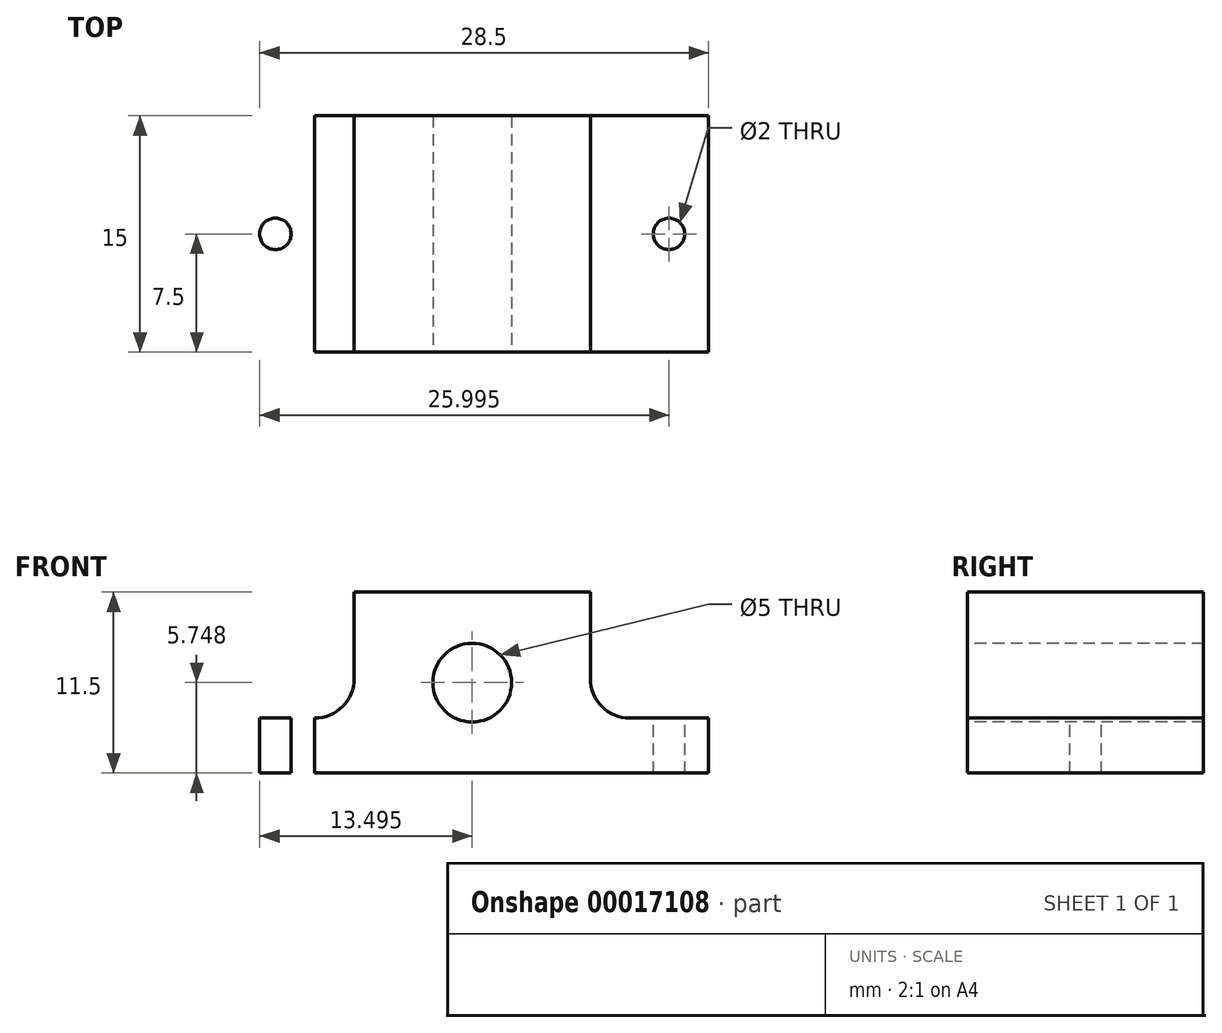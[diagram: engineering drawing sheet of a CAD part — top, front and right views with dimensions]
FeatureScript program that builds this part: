
annotation { "Feature Type Name" : "Feature", "Feature Type Description" : "" }
export const myFeature = defineFeature(function(context is Context, id is Id, definition is map)
    precondition{}
    {
        {
            var Q0;
            Q0=qCreatedBy(makeId("Front.planeOp"),FACE);
            var sketch = newSketch(context, id + "F0", { "sketchPlane" : qUnion([Q0])});
            skLineSegment(sketch, "E0", {"start": v(-8.65, 8.43) * mm, "end": v(6.35, 8.43) * mm});
            skLineSegment(sketch, "E1", {"start": v(6.35, 8.43) * mm, "end": v(6.35, 2.93) * mm});
            skLineSegment(sketch, "E2", {"start": v(8.85, 0.43) * mm, "end": v(13.85, 0.43) * mm});
            skLineSegment(sketch, "E3", {"start": v(13.85, 0.43) * mm, "end": v(13.85, -3.07) * mm});
            skLineSegment(sketch, "E4", {"start": v(-8.65, 8.43) * mm, "end": v(-8.65, 2.93) * mm});
            skLineSegment(sketch, "E5", {"start": v(-11.15, 0.43) * mm, "end": v(-16.15, 0.43) * mm});
            skLineSegment(sketch, "E6", {"start": v(-16.15, 0.43) * mm, "end": v(-16.15, -3.07) * mm});
            skLineSegment(sketch, "E7", {"start": v(-16.15, -3.07) * mm, "end": v(13.85, -3.07) * mm});
            skPoint(sketch, "E8.visualSharp", {"position": v(6.35, 0.43) * mm});
            skArc(sketch, "E8.filletArc", {"start": v(6.35, 2.93) * mm, "mid": v(7.08, 1.16) * mm, "end": v(8.85, 0.43) * mm});
            skPoint(sketch, "E9.visualSharp", {"position": v(-8.65, 0.43) * mm});
            skArc(sketch, "E9.filletArc", {"start": v(-11.15, 0.43) * mm, "mid": v(-9.39, 1.16) * mm, "end": v(-8.65, 2.93) * mm});
            skSolve(sketch);
        }
        {
            var Q0;
            Q0=makeQuery(id+"F0.imprint","IMPRINT",FACE,{"disambiguationData":[TD([[makeQuery(id+"F0.imprint","IMPRINT",EDGE,{"derivedFrom":sQuery(id+"F0.wireOp",EDGE,"E0")}),-1.0]])]});
            extrude(context, id + "F1", {"entities" : qUnion([Q0]), "depth" : 15 * mm});
        }
        {
            var Q0;
            Q0=makeQuery(id+"F1.opExtrude","SWEPT_FACE",FACE,{"disambiguationData":[OSD([sQuery(id+"F0.wireOp",EDGE,"E2")])]});
            var sketch = newSketch(context, id + "F2", { "sketchPlane" : qUnion([Q0])});
            skCircle(sketch, "E10", {"center": v(11.35, -7.5) * mm, "radius": 1 * mm});
            skSolve(sketch);
        }
        {
            var Q0;
            Q0 = qSketchRegion(id + "F2", true);
            extrude(context, id + "F3", {"entities" : qUnion([Q0]), "operationType" : NewBodyOperationType.REMOVE, "oppositeDirection" : true, "depth" : 5 * mm});
        }
        {
            var Q0;
            Q0=makeQuery(id+"F1.opExtrude","SWEPT_FACE",FACE,{"disambiguationData":[OSD([sQuery(id+"F0.wireOp",EDGE,"E5")])]});
            var sketch = newSketch(context, id + "F4", { "sketchPlane" : qUnion([Q0])});
            skLineSegment(sketch, "E11", {"start": v(-13.65, -15) * mm, "end": v(-13.65, 0) * mm});
            skCircle(sketch, "E12", {"center": v(-13.65, -7.5) * mm, "radius": 1 * mm});
            skSolve(sketch);
        }
        {
            var Q0;
            {var subQ0=sQuery(id+"F4.wireOp",EDGE,"E12");var subQ1=sQuery(id+"F4.wireOp",EDGE,"E11");var subQ3=makeQuery(id+"F4.imprint","INTERSECT",VERTEX,{"disambiguationData":[OD(0.0)],"derivedFrom":[subQ1,subQ0]});Q0=makeQuery(id+"F4.imprint","IMPRINT",FACE,{"disambiguationData":[TD([[makeQuery(id+"F4.imprint","IMPRINT",EDGE,{"disambiguationData":[TD([[subQ3,-1.0]])],"derivedFrom":subQ1}),1.0]])]});}
            var Q1;
            {var subQ0=sQuery(id+"F4.wireOp",EDGE,"E12");var subQ1=sQuery(id+"F4.wireOp",EDGE,"E11");var subQ3=makeQuery(id+"F4.imprint","INTERSECT",VERTEX,{"disambiguationData":[OD(0.0)],"derivedFrom":[subQ1,subQ0]});Q1=makeQuery(id+"F4.imprint","IMPRINT",FACE,{"disambiguationData":[TD([[makeQuery(id+"F4.imprint","IMPRINT",EDGE,{"disambiguationData":[TD([[subQ3,-1.0]])],"derivedFrom":subQ1}),-1.0]])]});}
            extrude(context, id + "F5", {"entities" : qUnion([Q0, Q1]), "operationType" : NewBodyOperationType.REMOVE, "endBound" : BoundingType.THROUGH_ALL, "oppositeDirection" : true, "depth" : 25 * mm});
        }
        {
            var Q0;
            Q0=makeQuery(id+"F1.opExtrude","CAP_FACE",FACE,{"disambiguationData":[OSD([sQuery(id+"F0.wireOp",EDGE,"E0"),sQuery(id+"F0.wireOp",EDGE,"E1"),sQuery(id+"F0.wireOp",EDGE,"E2"),sQuery(id+"F0.wireOp",EDGE,"E3"),sQuery(id+"F0.wireOp",EDGE,"E4"),sQuery(id+"F0.wireOp",EDGE,"E5"),sQuery(id+"F0.wireOp",EDGE,"E6"),sQuery(id+"F0.wireOp",EDGE,"E7"),sQuery(id+"F0.wireOp",EDGE,"E8.filletArc"),sQuery(id+"F0.wireOp",EDGE,"E9.filletArc")])],"isStart":false});
            var sketch = newSketch(context, id + "F6", { "sketchPlane" : qUnion([Q0])});
            skLineSegment(sketch, "E13", {"start": v(-1.15, 8.43) * mm, "end": v(-1.15, -3.07) * mm});
            skCircle(sketch, "E14", {"center": v(-1.15, 2.68) * mm, "radius": 2.5 * mm});
            skSolve(sketch);
        }
        {
            var Q0;
            Q0 = qSketchRegion(id + "F6", true);
            extrude(context, id + "F7", {"entities" : qUnion([Q0]), "operationType" : NewBodyOperationType.REMOVE, "endBound" : BoundingType.THROUGH_ALL, "oppositeDirection" : true, "depth" : 25 * mm});
        }
    });
